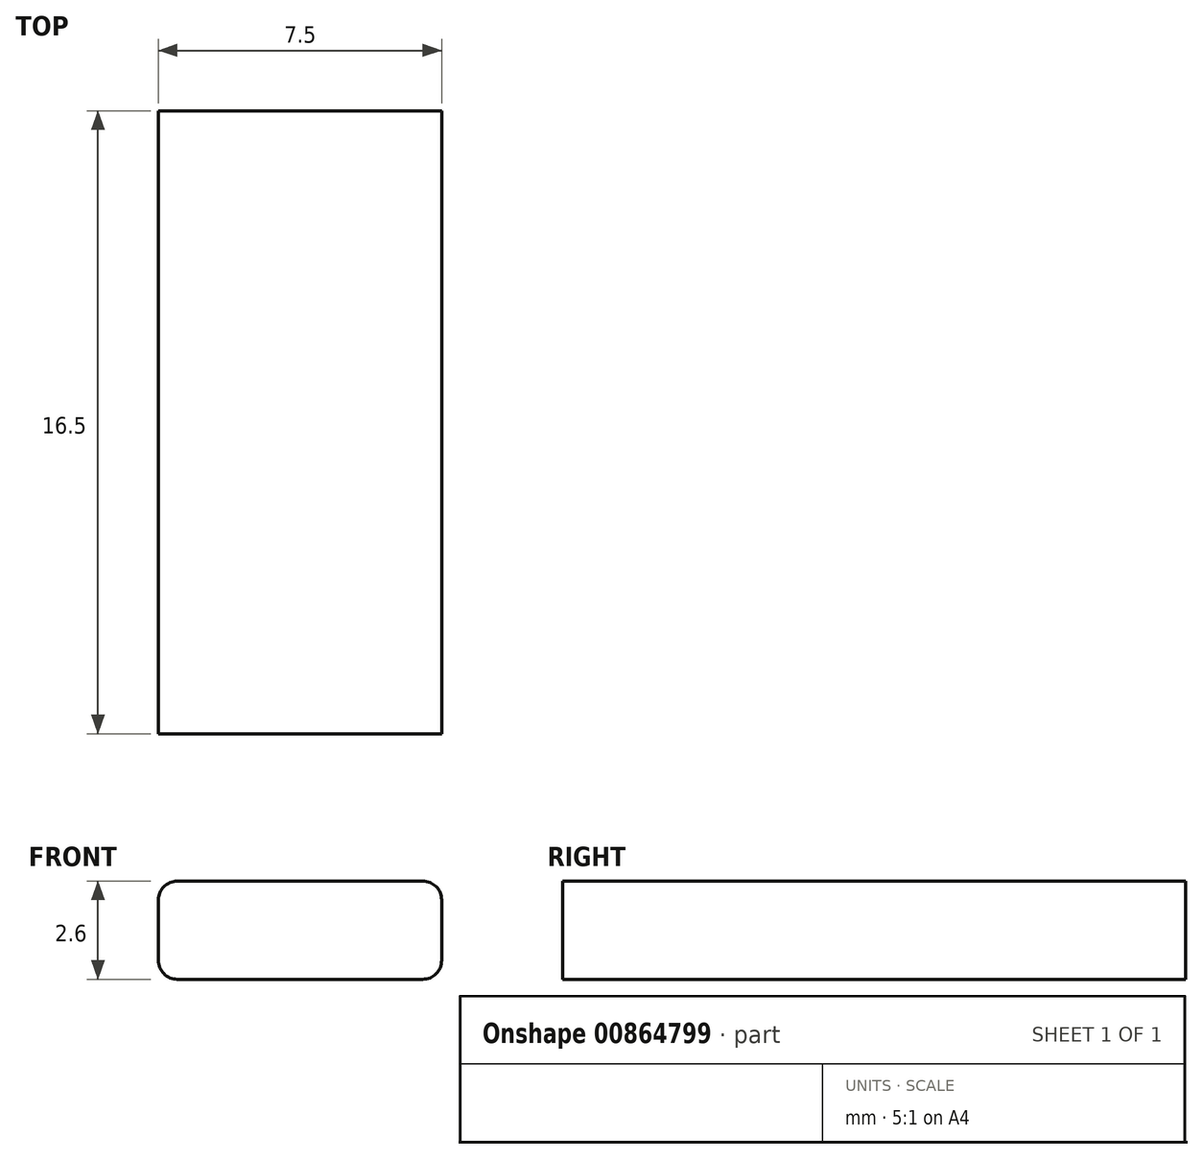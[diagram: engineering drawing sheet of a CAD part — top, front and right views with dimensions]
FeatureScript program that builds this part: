
annotation { "Feature Type Name" : "Feature", "Feature Type Description" : "" }
export const myFeature = defineFeature(function(context is Context, id is Id, definition is map)
    precondition{}
    {
        {
            var Q0;
            Q0=qCreatedBy(makeId("Top.planeOp"),FACE);
            var sketch = newSketch(context, id + "F0", { "sketchPlane" : qUnion([Q0])});
            skLineSegment(sketch, "E0.bottom", {"start": v(0, 0) * mm, "end": v(-7.5, 0) * mm});
            skLineSegment(sketch, "E0.top", {"start": v(0, 16.5) * mm, "end": v(-7.5, 16.5) * mm});
            skLineSegment(sketch, "E0.left", {"start": v(0, 0) * mm, "end": v(0, 16.5) * mm});
            skLineSegment(sketch, "E0.right", {"start": v(-7.5, 0) * mm, "end": v(-7.5, 16.5) * mm});
            skSolve(sketch);
        }
        {
            var Q0;
            Q0 = qSketchRegion(id + "F0", true);
            extrude(context, id + "F1", {"entities" : qUnion([Q0]), "depth" : 2.6 * mm, "offsetDistance" : 25 * mm});
        }
        {
            var Q0;
            Q0=makeQuery(id+"F1.opExtrude","CAP_EDGE",EDGE,{"disambiguationData":[OSD([sQuery(id+"F0.wireOp",EDGE,"E0.left")])],"isStart":false});
            var Q1;
            Q1=makeQuery(id+"F1.opExtrude","CAP_EDGE",EDGE,{"disambiguationData":[OSD([sQuery(id+"F0.wireOp",EDGE,"E0.right")])],"isStart":false});
            var Q2;
            Q2=makeQuery(id+"F1.opExtrude","CAP_EDGE",EDGE,{"disambiguationData":[OSD([sQuery(id+"F0.wireOp",EDGE,"E0.left")])],"isStart":true});
            var Q3;
            Q3=makeQuery(id+"F1.opExtrude","CAP_EDGE",EDGE,{"disambiguationData":[OSD([sQuery(id+"F0.wireOp",EDGE,"E0.right")])],"isStart":true});
            fillet(context, id + "F2", {"entities" : qUnion([Q0, Q1, Q2, Q3]), "radius" : 0.5 * mm, "tangentPropagation" : true, "allowEdgeOverflow" : false});
        }
    });
